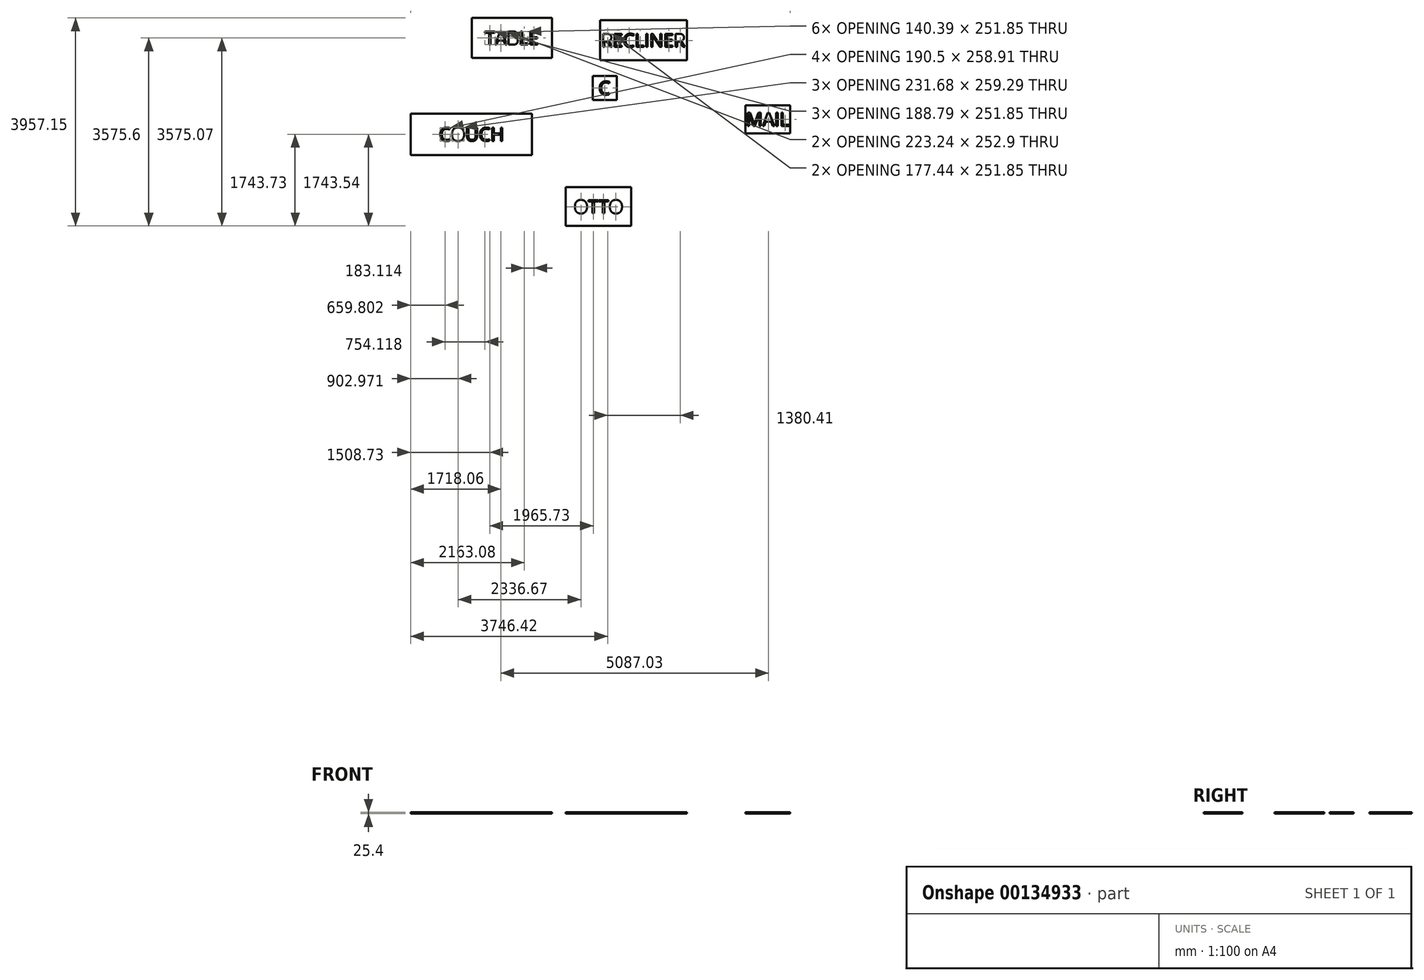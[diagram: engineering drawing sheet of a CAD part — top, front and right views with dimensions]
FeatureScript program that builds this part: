
annotation { "Feature Type Name" : "Feature", "Feature Type Description" : "" }
export const myFeature = defineFeature(function(context is Context, id is Id, definition is map)
    precondition{}
    {
        {
            var Q0;
            Q0=qCreatedBy(makeId("Top.planeOp"),FACE);
            var sketch = newSketch(context, id + "F0", { "sketchPlane" : qUnion([Q0])});
            skLineSegment(sketch, "E0.bottom", {"start": v(-1261.45, 147.23) * mm, "end": v(-3572.85, 147.23) * mm});
            skLineSegment(sketch, "E0.top", {"start": v(-1261.45, -640.17) * mm, "end": v(-3572.85, -640.17) * mm});
            skLineSegment(sketch, "E0.left", {"start": v(-1261.45, 147.23) * mm, "end": v(-1261.45, -640.17) * mm});
            skLineSegment(sketch, "E0.right", {"start": v(-3572.85, 147.23) * mm, "end": v(-3572.85, -640.17) * mm});
            skPoint(sketch, "E0.middle", {"position": v(-2417.15, -246.47) * mm});
            skLineSegment(sketch, "E1.bottom", {"start": v(622.3, -1254.43) * mm, "end": v(-622.3, -1254.43) * mm});
            skLineSegment(sketch, "E1.top", {"start": v(622.3, -1991.03) * mm, "end": v(-622.3, -1991.03) * mm});
            skLineSegment(sketch, "E1.left", {"start": v(622.3, -1254.43) * mm, "end": v(622.3, -1991.03) * mm});
            skLineSegment(sketch, "E1.right", {"start": v(-622.3, -1254.43) * mm, "end": v(-622.3, -1991.03) * mm});
            skPoint(sketch, "E1.middle", {"position": v(0, -1622.73) * mm});
            skLineSegment(sketch, "E2.bottom", {"start": v(-885.6, 1204.12) * mm, "end": v(-2409.6, 1204.12) * mm});
            skLineSegment(sketch, "E2.top", {"start": v(-885.6, 1966.12) * mm, "end": v(-2409.6, 1966.12) * mm});
            skLineSegment(sketch, "E2.left", {"start": v(-885.6, 1204.12) * mm, "end": v(-885.6, 1966.12) * mm});
            skLineSegment(sketch, "E2.right", {"start": v(-2409.6, 1204.12) * mm, "end": v(-2409.6, 1966.12) * mm});
            skPoint(sketch, "E2.middle", {"position": v(-1647.6, 1585.12) * mm});
            skLineSegment(sketch, "E3.bottom", {"start": v(346.06, 862.87) * mm, "end": v(-111.14, 862.87) * mm});
            skLineSegment(sketch, "E3.top", {"start": v(346.06, 405.67) * mm, "end": v(-111.14, 405.67) * mm});
            skLineSegment(sketch, "E3.left", {"start": v(346.06, 862.87) * mm, "end": v(346.06, 405.67) * mm});
            skLineSegment(sketch, "E3.right", {"start": v(-111.14, 862.87) * mm, "end": v(-111.14, 405.67) * mm});
            skPoint(sketch, "E3.middle", {"position": v(117.46, 634.27) * mm});
            skLineSegment(sketch, "E4.bottom", {"start": v(1683.41, 1920.6) * mm, "end": v(32.41, 1920.6) * mm});
            skLineSegment(sketch, "E4.top", {"start": v(1683.41, 1158.6) * mm, "end": v(32.41, 1158.6) * mm});
            skLineSegment(sketch, "E4.left", {"start": v(1683.41, 1920.6) * mm, "end": v(1683.41, 1158.6) * mm});
            skLineSegment(sketch, "E4.right", {"start": v(32.41, 1920.6) * mm, "end": v(32.41, 1158.6) * mm});
            skPoint(sketch, "E4.middle", {"position": v(857.91, 1539.6) * mm});
            skText(sketch, "E5", { "text": "COUCH", "fontName": "OpenSans-Regular.ttf"});
            skText(sketch, "E6", { "text": "TABLE", "fontName": "OpenSans-Regular.ttf"});
            skText(sketch, "E7", { "text": "RECLINER", "fontName": "OpenSans-Regular.ttf"});
            skText(sketch, "E8", { "text": "C", "fontName": "OpenSans-Regular.ttf"});
            skText(sketch, "E9", { "text": "OTTO", "fontName": "OpenSans-Regular.ttf"});
            skLineSegment(sketch, "E10.bottom", {"start": v(3646.55, -228.66) * mm, "end": v(2795.65, -228.66) * mm});
            skLineSegment(sketch, "E10.top", {"start": v(3646.55, 304.74) * mm, "end": v(2795.65, 304.74) * mm});
            skLineSegment(sketch, "E10.left", {"start": v(3646.55, -228.66) * mm, "end": v(3646.55, 304.74) * mm});
            skLineSegment(sketch, "E10.right", {"start": v(2795.65, -228.66) * mm, "end": v(2795.65, 304.74) * mm});
            skPoint(sketch, "E10.middle", {"position": v(3221.1, 38.04) * mm});
            skText(sketch, "E11", { "text": "MAIL", "fontName": "OpenSans-Regular.ttf"});
            const initialGuessF0  = {"E5": [-3.02985, -0.37347, 1, 0, 0.254], "E6": [-2.1616, 1.45812, 1, 0, 0.254], "E7": [0.05024, 1.4126, 1, 0, 0.254], "E8": [0, 0.50727, 1, 0, 0.254], "E9": [-0.4706, -1.74973, 1, 0, 0.254], "E11": [2.80212, -0.08896, 1, 0, 0.254]};
            skSetInitialGuess(sketch, initialGuessF0);
            skSolve(sketch);
        }
        {
            var Q0;
            Q0=makeQuery(id+"F0.imprint","IMPRINT",FACE,{"disambiguationData":[TD([[makeQuery(id+"F0.imprint","IMPRINT",EDGE,{"derivedFrom":sQuery(id+"F0.wireOp",EDGE,"E2.bottom")}),-1.0]])]});
            var Q1;
            Q1=makeQuery(id+"F0.imprint","IMPRINT",FACE,{"disambiguationData":[TD([[makeQuery(id+"F0.imprint","IMPRINT",EDGE,{"derivedFrom":sQuery(id+"F0.wireOp",EDGE,"E4.bottom")}),1.0]])]});
            var Q2;
            Q2=makeQuery(id+"F0.imprint","IMPRINT",FACE,{"disambiguationData":[TD([[makeQuery(id+"F0.imprint","IMPRINT",EDGE,{"derivedFrom":sQuery(id+"F0.wireOp",EDGE,"E3.bottom")}),1.0]])]});
            var Q3;
            Q3=makeQuery(id+"F0.imprint","IMPRINT",FACE,{"disambiguationData":[TD([[makeQuery(id+"F0.imprint","IMPRINT",EDGE,{"derivedFrom":sQuery(id+"F0.wireOp",EDGE,"E0.bottom")}),1.0]])]});
            var Q4;
            Q4=makeQuery(id+"F0.imprint","IMPRINT",FACE,{"disambiguationData":[TD([[makeQuery(id+"F0.imprint","IMPRINT",EDGE,{"derivedFrom":sQuery(id+"F0.wireOp",EDGE,"E1.bottom")}),1.0]])]});
            var Q5;
            Q5=makeQuery(id+"F0.imprint","IMPRINT",FACE,{"disambiguationData":[TD([[makeQuery(id+"F0.imprint","IMPRINT",EDGE,{"derivedFrom":sQuery(id+"F0.wireOp",EDGE,"E10.bottom")}),-1.0]])]});
            extrude(context, id + "F1", {"entities" : qUnion([Q0, Q1, Q2, Q3, Q4, Q5]), "depth" : 25.4 * mm});
        }
    });
